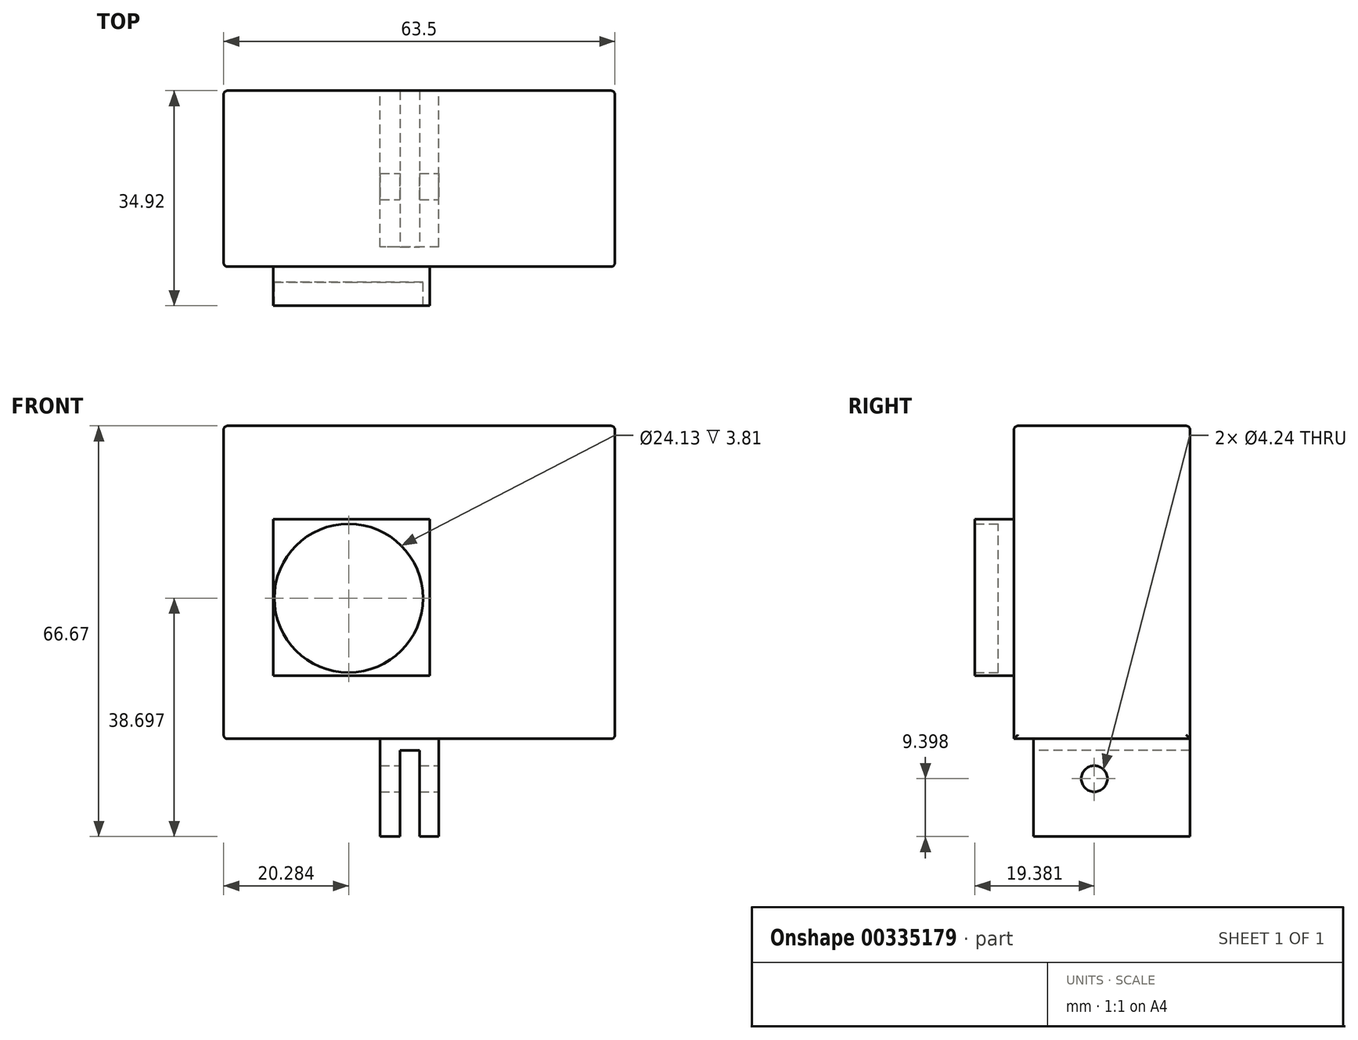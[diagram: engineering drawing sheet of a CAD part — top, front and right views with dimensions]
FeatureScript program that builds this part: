
annotation { "Feature Type Name" : "Feature", "Feature Type Description" : "" }
export const myFeature = defineFeature(function(context is Context, id is Id, definition is map)
    precondition{}
    {
        {
            var Q0;
            Q0=qCreatedBy(makeId("Right.planeOp"),FACE);
            var sketch = newSketch(context, id + "F0", { "sketchPlane" : qUnion([Q0])});
            skLineSegment(sketch, "E0.bottom", {"start": v(-19.47, 24.27) * mm, "end": v(9.1, 24.27) * mm});
            skLineSegment(sketch, "E0.top", {"start": v(-19.47, -26.53) * mm, "end": v(9.1, -26.53) * mm});
            skLineSegment(sketch, "E0.left", {"start": v(-19.47, 24.27) * mm, "end": v(-19.47, -26.53) * mm});
            skLineSegment(sketch, "E0.right", {"start": v(9.1, 24.27) * mm, "end": v(9.1, -26.53) * mm});
            skSolve(sketch);
        }
        {
            var Q0;
            Q0 = qSketchRegion(id + "F0", true);
            extrude(context, id + "F1", {"entities" : qUnion([Q0]), "depth" : 63.5 * mm});
        }
        {
            var Q0;
            Q0=makeQuery(id+"F1.opExtrude","SWEPT_FACE",FACE,{"disambiguationData":[OSD([sQuery(id+"F0.wireOp",EDGE,"E0.right")])]});
            var sketch = newSketch(context, id + "F2", { "sketchPlane" : qUnion([Q0])});
            skLineSegment(sketch, "E1.bottom", {"start": v(-34.93, -26.53) * mm, "end": v(-25.4, -26.53) * mm});
            skLineSegment(sketch, "E1.top", {"start": v(-34.93, -42.4) * mm, "end": v(-25.4, -42.4) * mm});
            skLineSegment(sketch, "E1.left", {"start": v(-34.93, -26.53) * mm, "end": v(-34.93, -42.4) * mm});
            skLineSegment(sketch, "E1.right", {"start": v(-25.4, -26.53) * mm, "end": v(-25.4, -42.4) * mm});
            skSolve(sketch);
        }
        {
            var Q0;
            Q0 = qSketchRegion(id + "F2", true);
            extrude(context, id + "F3", {"entities" : qUnion([Q0]), "oppositeDirection" : true, "depth" : 25.4 * mm});
        }
        {
            var Q0;
            Q0=makeQuery(id+"F3.opExtrude","SWEPT_FACE",FACE,{"disambiguationData":[OSD([sQuery(id+"F2.wireOp",EDGE,"E1.left")])]});
            var sketch = newSketch(context, id + "F4", { "sketchPlane" : qUnion([Q0])});
            skCircle(sketch, "E2", {"center": v(-6.44, -33) * mm, "radius": 2.12 * mm});
            skSolve(sketch);
        }
        {
            var Q0;
            Q0 = qSketchRegion(id + "F4", true);
            extrude(context, id + "F5", {"entities" : qUnion([Q0]), "operationType" : NewBodyOperationType.REMOVE, "oppositeDirection" : true, "depth" : 25.4 * mm});
        }
        {
            var Q0;
            Q0=makeQuery(id+"F1.opExtrude","SWEPT_FACE",FACE,{"disambiguationData":[OSD([sQuery(id+"F0.wireOp",EDGE,"E0.left")])]});
            var sketch = newSketch(context, id + "F6", { "sketchPlane" : qUnion([Q0])});
            skLineSegment(sketch, "E3.bottom", {"start": v(8.05, 9.14) * mm, "end": v(33.45, 9.14) * mm});
            skLineSegment(sketch, "E3.top", {"start": v(8.05, -16.26) * mm, "end": v(33.45, -16.26) * mm});
            skLineSegment(sketch, "E3.left", {"start": v(8.05, 9.14) * mm, "end": v(8.05, -16.26) * mm});
            skLineSegment(sketch, "E3.right", {"start": v(33.45, 9.14) * mm, "end": v(33.45, -16.26) * mm});
            skCircle(sketch, "E4", {"center": v(20.28, -3.7) * mm, "radius": 12.07 * mm});
            skSolve(sketch);
        }
        {
            var Q0;
            Q0 = qSketchRegion(id + "F6", true);
            extrude(context, id + "F7", {"entities" : qUnion([Q0]), "operationType" : NewBodyOperationType.ADD, "depth" : 6.35 * mm});
        }
        {
            var Q0;
            Q0=makeQuery(id+"F7.boolean.opBoolean","SPLIT",FACE,{"disambiguationData":[TD([makeQuery(id+"F7.opExtrude","SWEPT_FACE",FACE,{"disambiguationData":[OSD([sQuery(id+"F6.wireOp",EDGE,"E4")])]})])],"derivedFrom":makeQuery(id+"F1.opExtrude","SWEPT_FACE",FACE,{"disambiguationData":[OSD([sQuery(id+"F0.wireOp",EDGE,"E0.left")])]})});
            extrude(context, id + "F8", {"entities" : qUnion([Q0]), "operationType" : NewBodyOperationType.ADD, "depth" : 2.54 * mm});
        }
        {
            var Q0;
            Q0=makeQuery(id+"F3.opExtrude","CAP_FACE",FACE,{"disambiguationData":[OSD([sQuery(id+"F2.wireOp",EDGE,"E1.bottom"),sQuery(id+"F2.wireOp",EDGE,"E1.top"),sQuery(id+"F2.wireOp",EDGE,"E1.left"),sQuery(id+"F2.wireOp",EDGE,"E1.right")])],"isStart":false});
            var sketch = newSketch(context, id + "F9", { "sketchPlane" : qUnion([Q0])});
            skLineSegment(sketch, "E5.bottom", {"start": v(28.64, -42.4) * mm, "end": v(31.82, -42.4) * mm});
            skLineSegment(sketch, "E5.top", {"start": v(28.64, -28.43) * mm, "end": v(31.82, -28.43) * mm});
            skLineSegment(sketch, "E5.left", {"start": v(28.64, -42.4) * mm, "end": v(28.64, -28.43) * mm});
            skLineSegment(sketch, "E5.right", {"start": v(31.82, -42.4) * mm, "end": v(31.82, -28.43) * mm});
            skSolve(sketch);
        }
        {
            var Q0;
            Q0 = qSketchRegion(id + "F9", true);
            extrude(context, id + "F10", {"entities" : qUnion([Q0]), "operationType" : NewBodyOperationType.REMOVE, "depth" : -25.4 * mm});
        }
        {
            var Q0;
            Q0=makeQuery(id+"F1.opExtrude","SWEPT_EDGE",EDGE,{"disambiguationData":[OSD([sQuery(id+"F0.wireOp",EDGE,"E0.bottom"),sQuery(id+"F0.wireOp",EDGE,"E0.right")])]});
            var Q1;
            Q1=makeQuery(id+"F1.opExtrude","CAP_EDGE",EDGE,{"disambiguationData":[OSD([sQuery(id+"F0.wireOp",EDGE,"E0.bottom")])],"isStart":true});
            var Q2;
            Q2=makeQuery(id+"F1.opExtrude","SWEPT_EDGE",EDGE,{"disambiguationData":[OSD([sQuery(id+"F0.wireOp",EDGE,"E0.bottom"),sQuery(id+"F0.wireOp",EDGE,"E0.left")])]});
            var Q3;
            Q3=makeQuery(id+"F1.opExtrude","CAP_EDGE",EDGE,{"disambiguationData":[OSD([sQuery(id+"F0.wireOp",EDGE,"E0.bottom")])],"isStart":false});
            var Q4;
            Q4=makeQuery(id+"F1.opExtrude","CAP_EDGE",EDGE,{"disambiguationData":[OSD([sQuery(id+"F0.wireOp",EDGE,"E0.left")])],"isStart":true});
            var Q5;
            Q5=makeQuery(id+"F1.opExtrude","CAP_EDGE",EDGE,{"disambiguationData":[OSD([sQuery(id+"F0.wireOp",EDGE,"E0.top")])],"isStart":true});
            var Q6;
            Q6=makeQuery(id+"F1.opExtrude","CAP_EDGE",EDGE,{"disambiguationData":[OSD([sQuery(id+"F0.wireOp",EDGE,"E0.right")])],"isStart":true});
            var Q7;
            Q7=makeQuery(id+"F1.opExtrude","CAP_EDGE",EDGE,{"disambiguationData":[OSD([sQuery(id+"F0.wireOp",EDGE,"E0.left")])],"isStart":false});
            var Q8;
            Q8=makeQuery(id+"F1.opExtrude","CAP_EDGE",EDGE,{"disambiguationData":[OSD([sQuery(id+"F0.wireOp",EDGE,"E0.right")])],"isStart":false});
            var Q9;
            Q9=makeQuery(id+"F1.opExtrude","CAP_EDGE",EDGE,{"disambiguationData":[OSD([sQuery(id+"F0.wireOp",EDGE,"E0.top")])],"isStart":false});
            fillet(context, id + "F11", {"entities" : qUnion([Q0, Q1, Q2, Q3, Q4, Q5, Q6, Q7, Q8, Q9]), "radius" : 0.64 * mm, "tangentPropagation" : true, "allowEdgeOverflow" : false});
        }
    });
